# Revit family: CENTUM Gleiter GL-100 mit Grundplatte (2xM16 u.2xHalbzoll)
name_source: partatom
category: HLS-Bauteile
units: mm (PartAtom-declared; Revit-internal decimal feet)

## family parameters
Arbeitsebenenbasiert = Ja
Beim Laden mit Abzugskörper schneiden = Nein
Bemaßung runder Anschluss = Durchmesser verwenden
Beschriftungsausrichtung beibehalten = Nein
Gemeinsam genutzt = Ja
Immer vertikal = Nein
Klassifizierung = Keine
Raumberechnungspunkt = Nein
Teiletyp = Normal

## types (2) — shared parameters
Anzahl Anschlüsse = 2
Fabrikat = MEFA
Firma = MEFA Befestigungs- und Montagesysteme GmbH
Hersteller = MEFA
Kurztext1 = Gleiter axial für CENTUM
Material = Stahl
Material Gleitstreifen = Kunststoff
Materialname = S235
Materialname Gleitstreifen = Polyamid 6
Mengeneinheit = St
Profiltyp = XL 80, XL 100, XL 120 und XL 200
Vorgabe-Ansicht = 1219 mm
max. Schiebeweg axial = 75 mm
max. Temperaturbeständigkeit = 110 °C
vpe = 1

## per-type parameters (varying)
| type | Artikelnummer | EAN | Gewicht | Gewicht pro Bauteil | Gewicht pro Stück | Gewinde | Gleiter GL100 | Kurztext2 |
| Gleiter GL-100 m. Lasche 2xM16 | 0770565-01 | 4250928465962 | 1.82 kg | 1.82 kg | 1.82 kg | M16 | Gleiter GL-100 m.Lasche, 2xAG(M16 und Halbzoll) : Gleiter GL-100 m. Lasche, 2x M16 | Anschluss 2 x M16 |
| Gleiter GL-100 m. Lasche 2xHalbzoll | 0770611-01 | 4250928465979 | 1.26 kg | 1.26 kg | 1.26 kg | 1/2'' | Gleiter GL-100 m.Lasche, 2xAG(M16 und Halbzoll) : Gleiter GL-100 m. Lasche, 2x 1/2" | Anschluss 2 x 1/2'' |

## geometry (parser evidence)
native form markers: Sweep x2
no freeform markers — native parametric forms only
